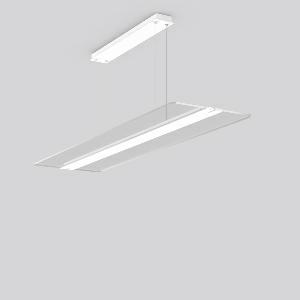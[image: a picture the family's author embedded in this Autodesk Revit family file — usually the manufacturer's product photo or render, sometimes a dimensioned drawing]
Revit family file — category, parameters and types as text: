
# Revit family: twindot_s_312263_002_1_730_9ce9
name_source: partatom
category: Lighting Fixtures
units: mm (PartAtom-declared; Revit-internal decimal feet)

## family parameters
Cut with Voids When Loaded = No
Host = Face
Light Source = No
Part Type = Normal
Room Calculation Point = No
Round Connector Dimension = Use Diameter
Shared = No

## types (1)
- TWINDOT S (1 x LED Modul 840, 6500 lm, 4000)
    Apparent Load = 54 VA
    CIE Flux Codes = 47 77 94 55 100
    Color Rendering = 80
    Color Temperature = 4000
    Default Elevation = 1800 mm
    Description = Series: TWINDOT S
LED pendant luminaire with extremely flat and frameless appearance. Middle bar made of aluminium extrusion profile, powder-coated. Transparent light guide made of UV-resistant acrylic glass (PMMA) with TWINDOT prismatic. Light control with perfectly glare-free TWINDOT technology for pleasantly gentle light with soft shadows. Even and wide indirect and direct light distribution. Direct 55%, indirect 45% light emission. 4-point steel cable suspension, steplessly adjustable. Converter integrated in the canopy (powder-coated white). Power supply through suspension cable. 
Colour: traffic white, matt (RAL 9016)
Length: 1200 mm
Width: 350 mm
Height: 20 mm
Suspension length: 500-1200 mm
Lamp: LED
Socket: without socket
Colour temperature: 4000K
Colour rendering index (CRI): 80
System power: 54 W
Rated luminous flux: 6500 lm
Luminous efficiency: 120 lm/W
Control gear: Dimmable Bluetooth converter
Protection class: I
Type of protection: IP 20
    Height = 20 mm
    Lamp = 1 x LED Modul 840
    Lamp Light Flux = 6500 lm
    Lamp count = 1
    Length = 1200 mm
    Lifetime = 50000 h
    Luminous efficacy = 120 lm/W
    Manufacturer = RZB
    ModVariant = No
    Model = 312263.002.1.730
    Mounting Place = Ceiling
    Mounting Type = Pendant
    Number of Poles = 1
    OnlyDefault = Yes
    Power Factor = 1
    Product Name = TWINDOT S
    Product group = Pendant modular luminaires
    ProductGroupID = 906
    Protection Class = Protection class I
    Protection Degree = IP 20
    RLX_Detail_Level = 1
    RLX_Emergency_Light_Flux = 0 lm
    RLX_Emergency_Type = 0
    RLX_Emergency_Type_DB = No
    RlxData = <blob elided: 35273 chars, md5=79832cf6>
    Socket = socket
    Standby Power = 0 W
    System Light Flux = 6500 lm
    System Power = 54 W
    Type Comments = Product without accessories
    Type Image = 312263.002.jpg
    URL = http://relux.com
    VarID = ---
    Voltage = 230 V
    Voltage Range = 220-240 V
    Weight = 0.00 kg
    Width = 350 mm

## geometry (parser evidence)
native form markers: Blend x4, Sweep x10
no freeform markers — native parametric forms only
